FCSTD DOCUMENT  (FreeCAD 1.0R39109 (Git))
Label: 1
License: All rights reserved
LicenseURL: https://en.wikipedia.org/wiki/All_rights_reserved
objects: App::Link×6, App::FeaturePython×6, Assembly::JointGroup×1, Assembly::AssemblyObject×1
EXTERNAL_REF file=../СР 6/2.FCStd obj=Body
EXTERNAL_REF file=../СР 6/Крышка.FCStd obj=Body
EXTERNAL_REF file=винт.FCStd obj=Screw

FEATURE [App::Link] ________  label="Тело"
  LinkedObject = -> <external ../СР 6/2.FCStd>#Body
FEATURE [App::FeaturePython] GroundedJoint  # Assembly grounded joint (typed FeaturePython)
  ObjectToGround = -> ________
FEATURE [App::Link] Body
  LinkPlacement = pos=(2.06e-14,1.685e-13,50) rot=(1,0,0;3.14159rad)
  LinkedObject = -> <external ../СР 6/Крышка.FCStd>#Body
  Placement = pos=(2.06e-14,1.685e-13,50) rot=(1,0,0;3.14159rad)
FEATURE [App::FeaturePython] Joint  label="Расстояние"  # Assembly joint (typed FeaturePython)
  Activated = true
  AngleMax = 0
  AngleMin = 0
  Detach1 = false
  Detach2 = false
  Distance = 0
  Distance2 = 0
  EnableAngleMax = false
  EnableAngleMin = false
  EnableLengthMax = false
  EnableLengthMin = false
  JointType = 5 (Distance)
  LengthMax = 0
  LengthMin = 0
  Placement1 = pos=(3.71e-14,2.945e-13,40) rot=(0,0,1;0rad)
  Placement2 = pos=(1.39e-14,-1.257e-13,10) rot=(0,0,1;0rad)
  Reference1 = -> Assembly [________.Face5,________.Vertex21]
  Reference2 = -> Assembly [Body.Face5,Body.Vertex27]
FEATURE [App::Link] M4x16_________  label="M4x16-Винт"
  LinkPlacement = pos=(103.75,65,47) rot=(0,0,1;0rad)
  LinkedObject = -> <external винт.FCStd>#Screw
  Placement = pos=(103.75,65,47) rot=(0,0,1;0rad)
FEATURE [App::Link] M4x16_________001  label="M4x16-Винт001"
  LinkPlacement = pos=(103.75,-65,47) rot=(0,0,1;0rad)
  LinkedObject = -> <external винт.FCStd>#Screw
  Placement = pos=(103.75,-65,47) rot=(0,0,1;0rad)
FEATURE [App::Link] M4x16_________002  label="M4x16-Винт002"
  LinkPlacement = pos=(-103.75,65,46.6) rot=(0,0,1;3.14159rad)
  LinkedObject = -> <external винт.FCStd>#Screw
  Placement = pos=(-103.75,65,46.6) rot=(0,0,1;3.14159rad)
FEATURE [App::Link] M4x16_________003  label="M4x16-Винт003"
  LinkPlacement = pos=(-103.75,-65,47) rot=(0,0,1;3.14159rad)
  LinkedObject = -> <external винт.FCStd>#Screw
  Placement = pos=(-103.75,-65,47) rot=(0,0,1;3.14159rad)
FEATURE [App::FeaturePython] Joint001  label="Цилиндрическое"  # Assembly joint (typed FeaturePython)
  Activated = true
  AngleMax = 0
  AngleMin = 0
  Detach1 = false
  Detach2 = false
  Distance = 0
  Distance2 = 0
  EnableAngleMax = false
  EnableAngleMin = false
  EnableLengthMax = false
  EnableLengthMin = false
  JointType = 2 (Cylindrical)
  LengthMax = 0
  LengthMin = 0
  Placement2 = pos=(103.75,-65,3) rot=(0,0,1;0rad)
  Reference1 = -> Assembly [M4x16_________.Edge26,M4x16_________.Edge26]
  Reference2 = -> Assembly [Body.Edge52,Body.Edge52]
FEATURE [App::FeaturePython] Joint002  label="Цилиндрическое001"  # Assembly joint (typed FeaturePython)
  Activated = true
  AngleMax = 0
  AngleMin = 0
  Detach1 = false
  Detach2 = false
  Distance = 0
  Distance2 = 0
  EnableAngleMax = false
  EnableAngleMin = false
  EnableLengthMax = false
  EnableLengthMin = false
  JointType = 2 (Cylindrical)
  LengthMax = 0
  LengthMin = 0
  Placement2 = pos=(103.75,65,3) rot=(0,0,1;0rad)
  Reference1 = -> Assembly [M4x16_________001.Edge26,M4x16_________001.Edge26]
  Reference2 = -> Assembly [Body.Edge72,Body.Edge72]
FEATURE [App::FeaturePython] Joint003  label="Цилиндрическое002"  # Assembly joint (typed FeaturePython)
  Activated = true
  AngleMax = 0
  AngleMin = 0
  Detach1 = false
  Detach2 = false
  Distance = 0
  Distance2 = 0
  EnableAngleMax = false
  EnableAngleMin = false
  EnableLengthMax = false
  EnableLengthMin = false
  JointType = 2 (Cylindrical)
  LengthMax = 0
  LengthMin = 0
  Placement1 = pos=(-103.75,-65,3) rot=(0,0,-1;3.14159rad)
  Placement2 = pos=(0,0,0.4) rot=(0,0,1;0rad)
  Reference1 = -> Assembly [Body.Edge50,Body.Edge50]
  Reference2 = -> Assembly [M4x16_________002.Edge12,M4x16_________002.Edge12]
FEATURE [App::FeaturePython] Joint004  label="Цилиндрическое003"  # Assembly joint (typed FeaturePython)
  Activated = true
  AngleMax = 0
  AngleMin = 0
  Detach1 = false
  Detach2 = false
  Distance = 0
  Distance2 = 0
  EnableAngleMax = false
  EnableAngleMin = false
  EnableLengthMax = false
  EnableLengthMin = false
  JointType = 2 (Cylindrical)
  LengthMax = 0
  LengthMin = 0
  Placement2 = pos=(-103.75,65,3) rot=(0,0,-1;3.14159rad)
  Reference1 = -> Assembly [M4x16_________003.Edge26,M4x16_________003.Edge26]
  Reference2 = -> Assembly [Body.Edge54,Body.Edge54]
FEATURE [Assembly::JointGroup] Joints
  Group = -> [GroundedJoint,Joint,Joint001,Joint002,Joint003,Joint004]
FEATURE [Assembly::AssemblyObject] Assembly
  Group = -> [Joints,________,GroundedJoint,Body,Joint,M4x16_________,M4x16_________001,M4x16_________002,M4x16_________003,Joint001,Joint002,Joint003,Joint004]
  Origin = -> Origin
  Type = Assembly
